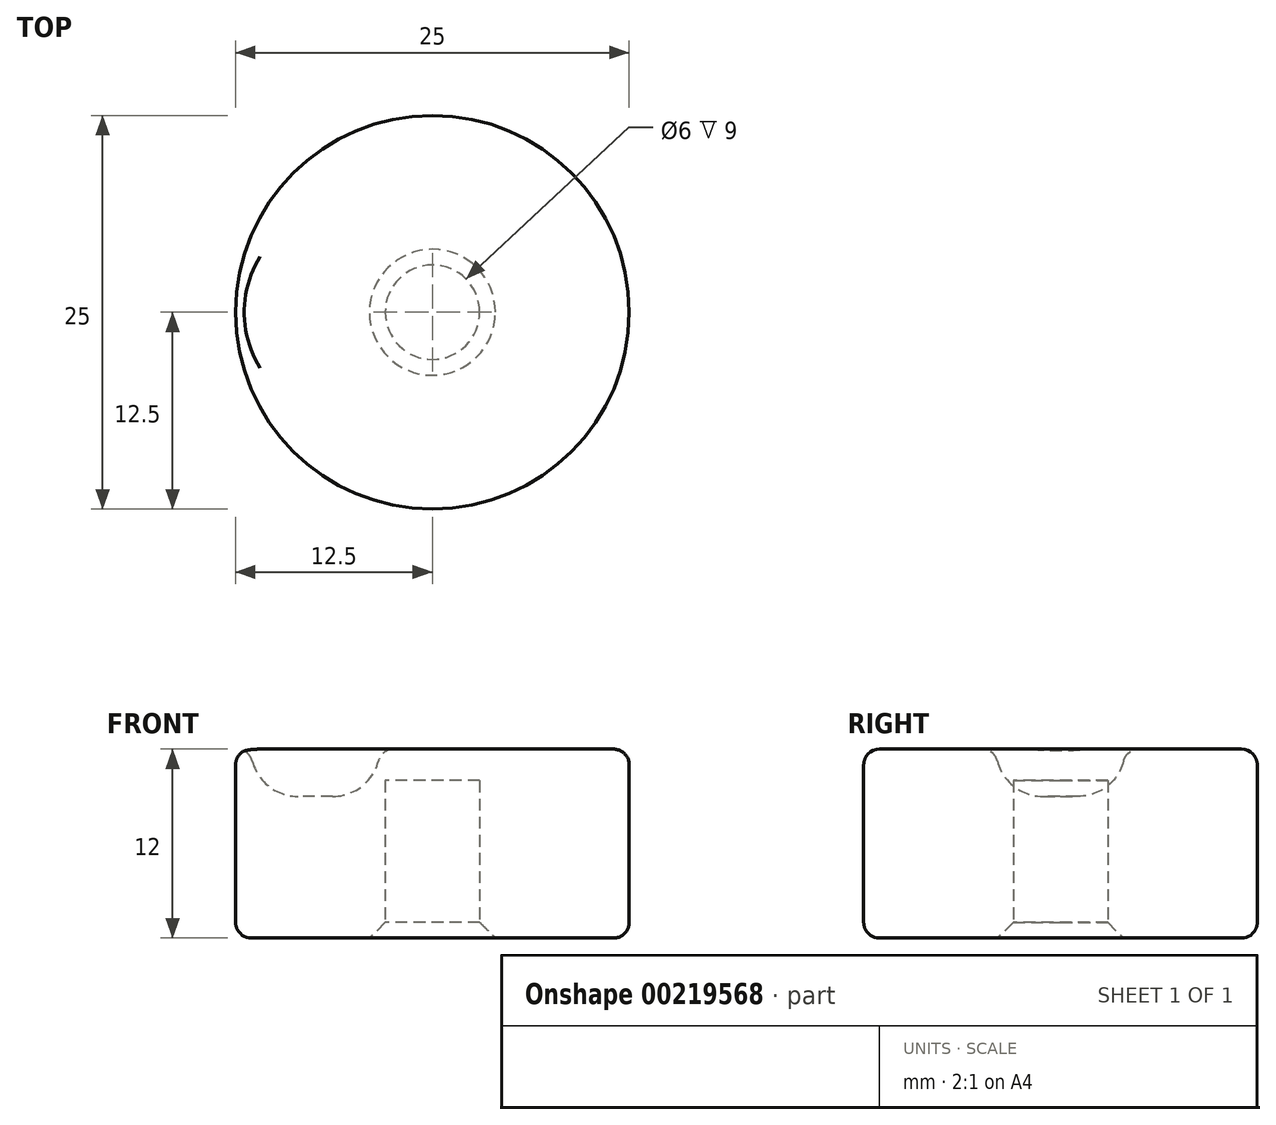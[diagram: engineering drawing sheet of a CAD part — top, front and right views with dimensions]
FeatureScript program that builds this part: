
annotation { "Feature Type Name" : "Feature", "Feature Type Description" : "" }
export const myFeature = defineFeature(function(context is Context, id is Id, definition is map)
    precondition{}
    {
        {
            var Q0;
            Q0=qCreatedBy(makeId("Top.planeOp"),FACE);
            var sketch = newSketch(context, id + "F0", { "sketchPlane" : qUnion([Q0])});
            skCircle(sketch, "E0", {"center": v(0, 0) * mm, "radius": 3 * mm});
            skCircle(sketch, "E1", {"center": v(0, 0) * mm, "radius": 12.5 * mm});
            skSolve(sketch);
        }
        {
            var Q0;
            Q0=makeQuery(id+"F0.imprint","IMPRINT",FACE,{"disambiguationData":[TD([[makeQuery(id+"F0.imprint","IMPRINT",EDGE,{"derivedFrom":sQuery(id+"F0.wireOp",EDGE,"E0")}),-1.0]])]});
            extrude(context, id + "F1", {"entities" : qUnion([Q0]), "depth" : 10 * mm});
        }
        {
            var Q0;
            Q0=makeQuery(id+"F1.opExtrude","CAP_FACE",FACE,{"disambiguationData":[OSD([sQuery(id+"F0.wireOp",EDGE,"E0"),sQuery(id+"F0.wireOp",EDGE,"E1")])],"isStart":false});
            var sketch = newSketch(context, id + "F2", { "sketchPlane" : qUnion([Q0])});
            skCircle(sketch, "E2", {"center": v(0, 0) * mm, "radius": 12.5 * mm});
            skSolve(sketch);
        }
        {
            var Q0;
            Q0=makeQuery(id+"F2.imprint","IMPRINT",FACE,{"disambiguationData":[TD([[makeQuery(id+"F2.imprint","IMPRINT",EDGE,{"derivedFrom":sQuery(id+"F2.wireOp",EDGE,"E2")}),1.0]])]});
            var Q1;
            Q1=makeQuery(id+"F2.imprint","IMPRINT",FACE,{"disambiguationData":[TD([[makeQuery(id+"F2.imprint","IMPRINT",EDGE,{"derivedFrom":makeQuery(id+"F1.opExtrude","CAP_EDGE",EDGE,{"disambiguationData":[OSD([sQuery(id+"F0.wireOp",EDGE,"E0")])],"isStart":false})}),1.0]])]});
            extrude(context, id + "F3", {"entities" : qUnion([Q0, Q1]), "operationType" : NewBodyOperationType.ADD, "depth" : 2 * mm});
        }
        {
            var Q0;
            Q0=makeQuery(id+"F3.opExtrude","CAP_FACE",FACE,{"disambiguationData":[OSD([sQuery(id+"F2.wireOp",EDGE,"E2")])],"isStart":false});
            var sketch = newSketch(context, id + "F4", { "sketchPlane" : qUnion([Q0])});
            skCircle(sketch, "E3", {"center": v(-7.44, 0) * mm, "radius": 4.1 * mm});
            skSolve(sketch);
        }
        {
            var Q0;
            Q0=makeQuery(id+"F4.imprint","IMPRINT",FACE,{"disambiguationData":[TD([[makeQuery(id+"F4.imprint","IMPRINT",EDGE,{"derivedFrom":sQuery(id+"F4.wireOp",EDGE,"E3")}),1.0]])]});
            extrude(context, id + "F5", {"entities" : qUnion([Q0]), "operationType" : NewBodyOperationType.REMOVE, "oppositeDirection" : true, "depth" : 3 * mm});
        }
        {
            var Q0;
            Q0=makeQuery(id+"F5.boolean.opBoolean","COPY",EDGE,{"derivedFrom":makeQuery(id+"F5.opExtrude","CAP_EDGE",EDGE,{"disambiguationData":[OSD([sQuery(id+"F4.wireOp",EDGE,"E3")])],"isStart":false})});
            fillet(context, id + "F6", {"entities" : qUnion([Q0]), "radius" : 3 * mm, "tangentPropagation" : true, "allowEdgeOverflow" : false});
        }
        {
            var Q0;
            Q0=makeQuery(id+"F3.opExtrude","CAP_FACE",FACE,{"disambiguationData":[OSD([sQuery(id+"F2.wireOp",EDGE,"E2")])],"isStart":false});
            fillet(context, id + "F7", {"entities" : qUnion([Q0]), "radius" : 1 * mm, "tangentPropagation" : true, "allowEdgeOverflow" : false});
        }
        {
            var Q0;
            Q0=makeQuery(id+"F1.opExtrude","CAP_EDGE",EDGE,{"disambiguationData":[OSD([sQuery(id+"F0.wireOp",EDGE,"E1")])],"isStart":true});
            fillet(context, id + "F8", {"entities" : qUnion([Q0]), "radius" : 1 * mm, "tangentPropagation" : true, "allowEdgeOverflow" : false});
        }
        {
            var Q0;
            Q0=makeQuery(id+"F1.opExtrude","CAP_EDGE",EDGE,{"disambiguationData":[OSD([sQuery(id+"F0.wireOp",EDGE,"E0")])],"isStart":true});
            chamfer(context, id + "F9", {"entities" : qUnion([Q0]), "width" : 1 * mm, "tangentPropagation" : true});
        }
    });
